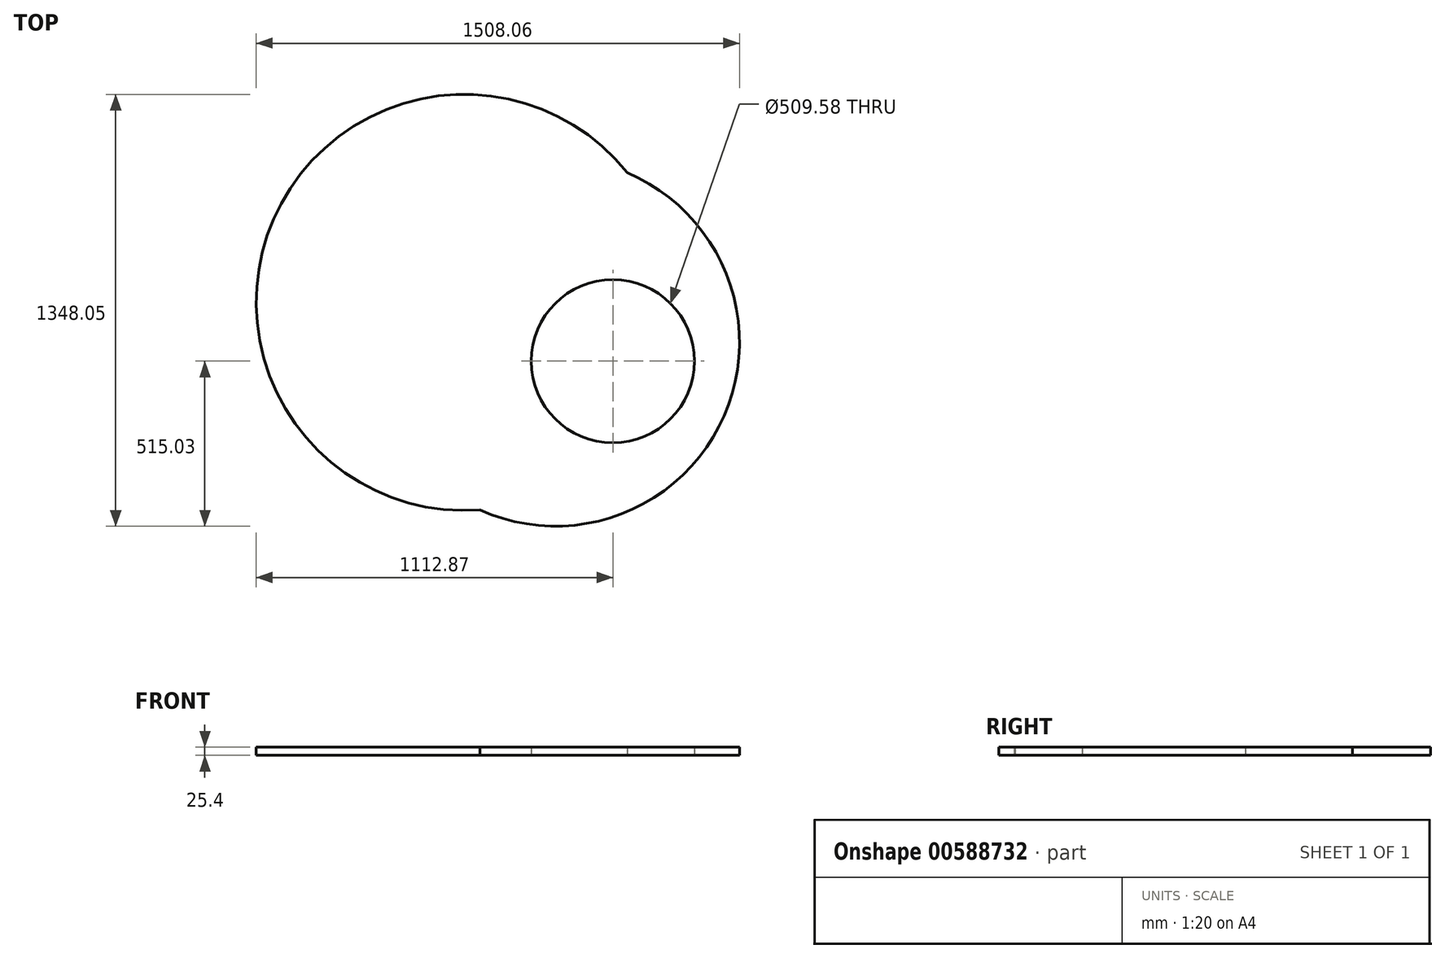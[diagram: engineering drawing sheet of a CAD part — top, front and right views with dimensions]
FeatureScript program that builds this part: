
annotation { "Feature Type Name" : "Feature", "Feature Type Description" : "" }
export const myFeature = defineFeature(function(context is Context, id is Id, definition is map)
    precondition{}
    {
        {
            var Q0;
            Q0=qCreatedBy(makeId("Top.planeOp"),FACE);
            var sketch = newSketch(context, id + "F0", { "sketchPlane" : qUnion([Q0])});
            skCircle(sketch, "E0", {"center": v(0, 0) * mm, "radius": 76.97 * mm});
            skCircle(sketch, "E1", {"center": v(0, 0) * mm, "radius": 11.06 * mm});
            skCircle(sketch, "E2", {"center": v(0, 0) * mm, "radius": 199.27 * mm});
            skCircle(sketch, "E3", {"center": v(-190.23, 59.34) * mm, "radius": 574.37 * mm});
            skCircle(sketch, "E4", {"center": v(-474.3, 183.4) * mm, "radius": 649.62 * mm});
            skCircle(sketch, "E5", {"center": v(-11.06, 0) * mm, "radius": 254.8 * mm});
            skSolve(sketch);
        }
        {
            var Q0;
            Q0 = qSketchRegion(id + "F0", true);
            extrude(context, id + "F1", {"entities" : qUnion([Q0]), "depth" : 25.4 * mm, "offsetDistance" : 25.4 * mm});
        }
    });
